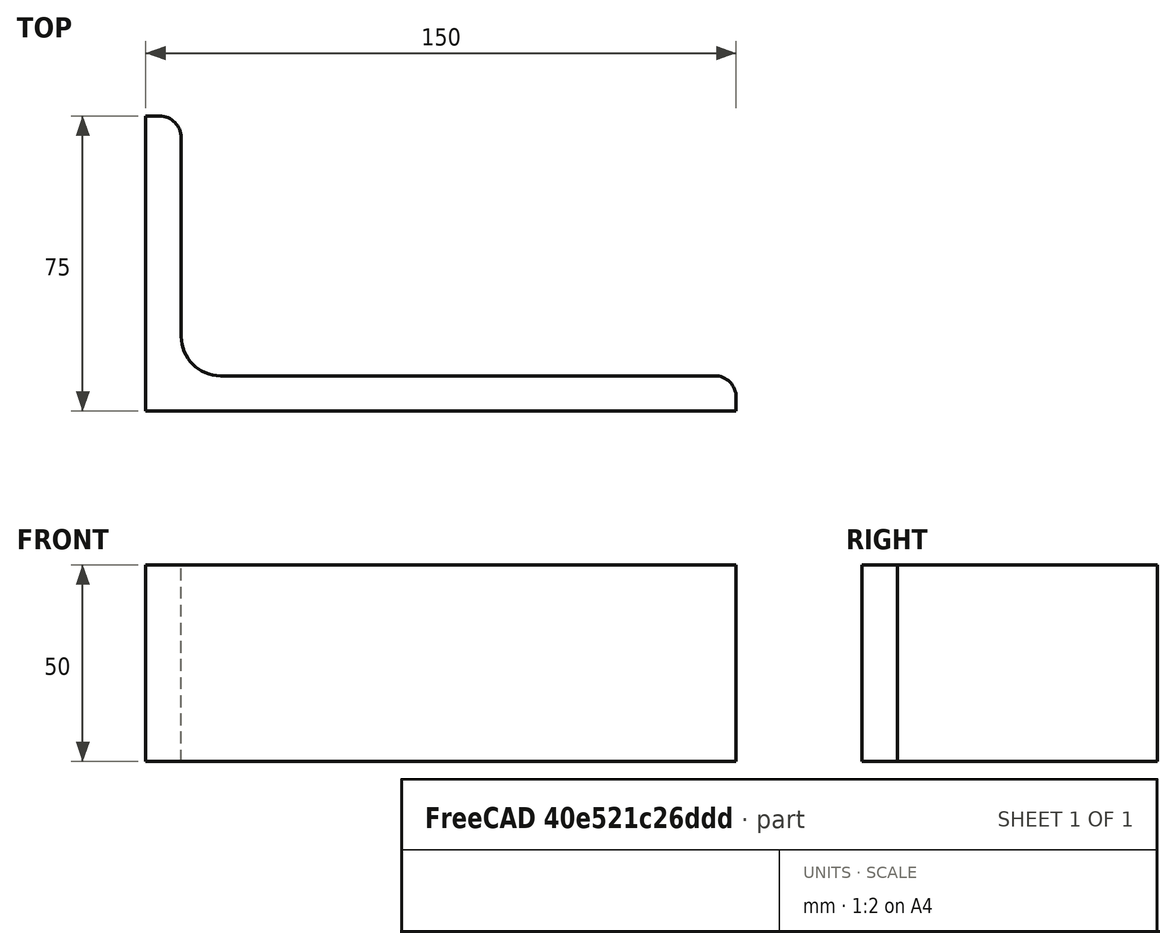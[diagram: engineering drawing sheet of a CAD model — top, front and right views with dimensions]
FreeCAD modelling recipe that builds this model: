
FCSTD DOCUMENT  (FreeCAD 0.15R4671 (Git))
Label: Angle Bar 150x75x9 EN10056 S235JR
License: All rights reserved
LicenseURL: http://en.wikipedia.org/wiki/All_rights_reserved
objects: Sketcher::SketchObject×1, Part::Extrusion×1
note: 2 computed .brp shape members not serialized (recipe doc carries the construction recipe); baked Part::Feature solids carry a one-line shape summary decoded from their .brp

FEATURE [Sketcher::SketchObject] Sketch
  sketch-geometry (9):
    g0: LineSegment StartX=0 StartY=0 StartZ=0 EndX=150 EndY=0 EndZ=0
    g1: LineSegment StartX=150 StartY=0 StartZ=0 EndX=150 EndY=3.5 EndZ=0
    g2: LineSegment StartX=144.5 StartY=9 StartZ=0 EndX=19 EndY=9 EndZ=0
    g3: LineSegment StartX=0 StartY=0 StartZ=0 EndX=0 EndY=75 EndZ=0
    g4: LineSegment StartX=0 StartY=75 StartZ=0 EndX=3.5 EndY=75 EndZ=0
    g5: LineSegment StartX=9 StartY=69.5 StartZ=0 EndX=9 EndY=19 EndZ=0
    g6: ArcOfCircle CenterX=19 CenterY=19 CenterZ=0 NormalX=0 NormalY=0 NormalZ=1 Radius=10 StartAngle=3.14159 EndAngle=4.71239
    g7: ArcOfCircle CenterX=3.5 CenterY=69.5 CenterZ=0 NormalX=0 NormalY=0 NormalZ=1 Radius=5.5 StartAngle=0 EndAngle=1.5708
    g8: ArcOfCircle CenterX=144.5 CenterY=3.5 CenterZ=0 NormalX=0 NormalY=0 NormalZ=1 Radius=5.5 StartAngle=0 EndAngle=1.5708
  constraints (23):
    c: Coincident(g0,g-1)
    c: Horizontal(g0)
    c: Coincident(g1,g0)
    c: Vertical(g1)
    c: Horizontal(g2)
    c: Coincident(g3,g-1)
    c: Vertical(g3)
    c: Coincident(g4,g3)
    c: Horizontal(g4)
    c: Vertical(g5)
    c: Tangent(g5,g6) = -1.5708
    c: Tangent(g2,g6) = 1.5708
    c: Tangent(g4,g7) = 1.5708
    c: Tangent(g5,g7) = 1.5708
    c: Tangent(g2,g8) = -1.5708
    c: Tangent(g1,g8) = -1.5708
    c: DistanceX(g0) = 150
    c: DistanceY(g3) = 75
    c: DistanceY(g0,g2) = 9
    c: DistanceX(g3,g5) = 9
    c: Radius(g6) = 10
    c: Radius(g8) = 5.5
    c: Radius(g7) = 5.5
FEATURE [Part::Extrusion] Extrude  label="Angle Bar 150x75x9 EN10056 S235JR"
  Base = -> Sketch
  Dir = (0,0,50)
  Solid = true
